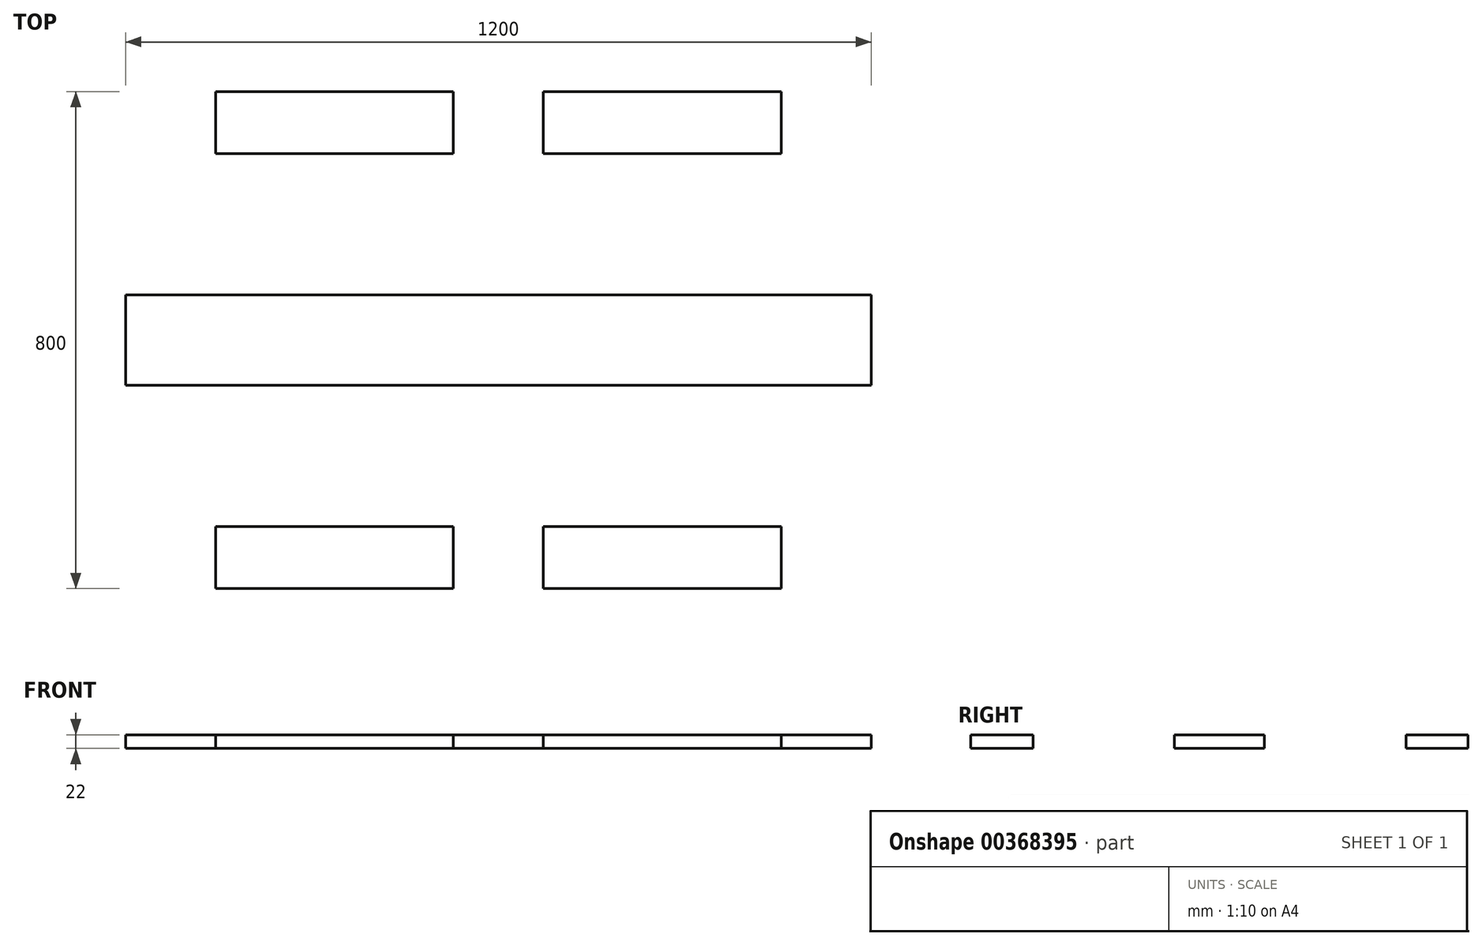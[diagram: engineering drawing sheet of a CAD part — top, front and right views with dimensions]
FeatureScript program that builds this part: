
annotation { "Feature Type Name" : "Feature", "Feature Type Description" : "" }
export const myFeature = defineFeature(function(context is Context, id is Id, definition is map)
    precondition{}
    {
        {
            var Q0;
            Q0=qCreatedBy(makeId("Top.planeOp"),FACE);
            var sketch = newSketch(context, id + "F0", { "sketchPlane" : qUnion([Q0])});
            skLineSegment(sketch, "E0.bottom", {"start": v(600, 400) * mm, "end": v(-600, 400) * mm, "construction": true});
            skLineSegment(sketch, "E0.top", {"start": v(600, -400) * mm, "end": v(-600, -400) * mm, "construction": true});
            skLineSegment(sketch, "E0.left", {"start": v(600, 400) * mm, "end": v(600, -400) * mm, "construction": true});
            skLineSegment(sketch, "E0.right", {"start": v(-600, 400) * mm, "end": v(-600, -400) * mm, "construction": true});
            skPoint(sketch, "E0.middle", {"position": v(0, 0) * mm});
            skLineSegment(sketch, "E1.left", {"start": v(-600, -400) * mm, "end": v(-600, -400) * mm});
            skLineSegment(sketch, "E1.right", {"start": v(600, -400) * mm, "end": v(600, -400) * mm});
            skLineSegment(sketch, "E2.bottom", {"start": v(-600, -400) * mm, "end": v(600, -400) * mm});
            skLineSegment(sketch, "E2.top", {"start": v(-600, -300) * mm, "end": v(600, -300) * mm});
            skLineSegment(sketch, "E2.left", {"start": v(-600, -400) * mm, "end": v(-600, -300) * mm});
            skLineSegment(sketch, "E2.right", {"start": v(600, -400) * mm, "end": v(600, -300) * mm});
            skLineSegment(sketch, "E3.bottom", {"start": v(-600, 400) * mm, "end": v(600, 400) * mm});
            skLineSegment(sketch, "E3.top", {"start": v(-600, 300) * mm, "end": v(600, 300) * mm});
            skLineSegment(sketch, "E3.left", {"start": v(-600, 400) * mm, "end": v(-600, 300) * mm});
            skLineSegment(sketch, "E3.right", {"start": v(600, 400) * mm, "end": v(600, 300) * mm});
            skLineSegment(sketch, "E4.bottom", {"start": v(-600, 72.5) * mm, "end": v(600, 72.5) * mm});
            skLineSegment(sketch, "E4.top", {"start": v(-600, -72.5) * mm, "end": v(600, -72.5) * mm});
            skLineSegment(sketch, "E4.left", {"start": v(-600, 72.5) * mm, "end": v(-600, -72.5) * mm});
            skLineSegment(sketch, "E4.right", {"start": v(600, 72.5) * mm, "end": v(600, -72.5) * mm});
            skLineSegment(sketch, "E5.bottom", {"start": v(-600, 260) * mm, "end": v(600, 260) * mm});
            skLineSegment(sketch, "E5.top", {"start": v(-600, 160) * mm, "end": v(600, 160) * mm});
            skLineSegment(sketch, "E5.left", {"start": v(-600, 260) * mm, "end": v(-600, 160) * mm});
            skLineSegment(sketch, "E5.right", {"start": v(600, 260) * mm, "end": v(600, 160) * mm});
            skLineSegment(sketch, "E6.bottom", {"start": v(-600, -160) * mm, "end": v(600, -160) * mm});
            skLineSegment(sketch, "E6.top", {"start": v(-600, -260) * mm, "end": v(600, -260) * mm});
            skLineSegment(sketch, "E6.left", {"start": v(-600, -160) * mm, "end": v(-600, -260) * mm});
            skLineSegment(sketch, "E6.right", {"start": v(600, -160) * mm, "end": v(600, -260) * mm});
            skLineSegment(sketch, "E7.bottom", {"start": v(-600, 400) * mm, "end": v(-455, 400) * mm});
            skLineSegment(sketch, "E7.top", {"start": v(-600, -400) * mm, "end": v(-455, -400) * mm});
            skLineSegment(sketch, "E7.left", {"start": v(-600, 400) * mm, "end": v(-600, -400) * mm});
            skLineSegment(sketch, "E7.right", {"start": v(-455, 400) * mm, "end": v(-455, -400) * mm});
            skLineSegment(sketch, "E8.bottom", {"start": v(600, 400) * mm, "end": v(455, 400) * mm});
            skLineSegment(sketch, "E8.top", {"start": v(600, -400) * mm, "end": v(455, -400) * mm});
            skLineSegment(sketch, "E8.left", {"start": v(600, 400) * mm, "end": v(600, -400) * mm});
            skLineSegment(sketch, "E8.right", {"start": v(455, 400) * mm, "end": v(455, -400) * mm});
            skLineSegment(sketch, "E9.bottom", {"start": v(72, -400) * mm, "end": v(-73, -400) * mm});
            skLineSegment(sketch, "E9.top", {"start": v(72, 400) * mm, "end": v(-73, 400) * mm});
            skLineSegment(sketch, "E9.left", {"start": v(72, -400) * mm, "end": v(72, 400) * mm});
            skLineSegment(sketch, "E9.right", {"start": v(-73, -400) * mm, "end": v(-73, 400) * mm});
            skPoint(sketch, "E9.middle", {"position": v(-0.5, 0) * mm});
            skSolve(sketch);
        }
        {
            var Q0;
            {var subQ5=sQuery(id+"F0.wireOp",EDGE,"E8.bottom");Q0=makeQuery(id+"F0.imprint","IMPRINT",FACE,{"disambiguationData":[TD([[makeQuery(id+"F0.imprint","IMPRINT",EDGE,{"derivedFrom":subQ5}),1.0]])]});}
            var Q1;
            {var subQ3=sQuery(id+"F0.wireOp",EDGE,"E9.left");var subQ5=sQuery(id+"F0.wireOp",EDGE,"E3.top");var subQ6=makeQuery(id+"F0.imprint","INTERSECT",VERTEX,{"derivedFrom":[subQ5,subQ3]});Q1=makeQuery(id+"F0.imprint","IMPRINT",FACE,{"disambiguationData":[TD([[makeQuery(id+"F0.imprint","IMPRINT",EDGE,{"disambiguationData":[TD([[subQ6,-1.0]])],"derivedFrom":subQ5}),1.0]])]});}
            var Q2;
            {var subQ5=sQuery(id+"F0.wireOp",EDGE,"E9.top");Q2=makeQuery(id+"F0.imprint","IMPRINT",FACE,{"disambiguationData":[TD([[makeQuery(id+"F0.imprint","IMPRINT",EDGE,{"derivedFrom":subQ5}),1.0]])]});}
            var Q3;
            {var subQ0=sQuery(id+"F0.wireOp",EDGE,"E7.right");var subQ5=sQuery(id+"F0.wireOp",EDGE,"E3.top");var subQ6=makeQuery(id+"F0.imprint","INTERSECT",VERTEX,{"derivedFrom":[subQ5,subQ0]});Q3=makeQuery(id+"F0.imprint","IMPRINT",FACE,{"disambiguationData":[TD([[makeQuery(id+"F0.imprint","IMPRINT",EDGE,{"disambiguationData":[TD([[subQ6,-1.0]])],"derivedFrom":subQ5}),1.0]])]});}
            var Q4;
            {var subQ5=sQuery(id+"F0.wireOp",EDGE,"E7.bottom");Q4=makeQuery(id+"F0.imprint","IMPRINT",FACE,{"disambiguationData":[TD([[makeQuery(id+"F0.imprint","IMPRINT",EDGE,{"derivedFrom":subQ5}),-1.0]])]});}
            var Q5;
            {var subQ0=sQuery(id+"F0.wireOp",EDGE,"E7.left");var subQ1=sQuery(id+"F0.wireOp",EDGE,"E5.bottom");var subQ2=makeQuery(id+"F0.imprint","INTERSECT",VERTEX,{"derivedFrom":[subQ1,subQ0]});Q5=makeQuery(id+"F0.imprint","IMPRINT",FACE,{"disambiguationData":[TD([[makeQuery(id+"F0.imprint","IMPRINT",EDGE,{"disambiguationData":[TD([[subQ2,-1.0]])],"derivedFrom":subQ1}),-1.0]])]});}
            var Q6;
            {var subQ0=sQuery(id+"F0.wireOp",EDGE,"E7.right");var subQ1=sQuery(id+"F0.wireOp",EDGE,"E5.bottom");var subQ2=makeQuery(id+"F0.imprint","INTERSECT",VERTEX,{"derivedFrom":[subQ1,subQ0]});Q6=makeQuery(id+"F0.imprint","IMPRINT",FACE,{"disambiguationData":[TD([[makeQuery(id+"F0.imprint","IMPRINT",EDGE,{"disambiguationData":[TD([[subQ2,-1.0]])],"derivedFrom":subQ1}),-1.0]])]});}
            var Q7;
            {var subQ0=sQuery(id+"F0.wireOp",EDGE,"E9.right");var subQ1=sQuery(id+"F0.wireOp",EDGE,"E5.bottom");var subQ2=makeQuery(id+"F0.imprint","INTERSECT",VERTEX,{"derivedFrom":[subQ1,subQ0]});Q7=makeQuery(id+"F0.imprint","IMPRINT",FACE,{"disambiguationData":[TD([[makeQuery(id+"F0.imprint","IMPRINT",EDGE,{"disambiguationData":[TD([[subQ2,-1.0]])],"derivedFrom":subQ1}),-1.0]])]});}
            var Q8;
            {var subQ0=sQuery(id+"F0.wireOp",EDGE,"E9.left");var subQ1=sQuery(id+"F0.wireOp",EDGE,"E5.bottom");var subQ2=makeQuery(id+"F0.imprint","INTERSECT",VERTEX,{"derivedFrom":[subQ1,subQ0]});Q8=makeQuery(id+"F0.imprint","IMPRINT",FACE,{"disambiguationData":[TD([[makeQuery(id+"F0.imprint","IMPRINT",EDGE,{"disambiguationData":[TD([[subQ2,-1.0]])],"derivedFrom":subQ1}),-1.0]])]});}
            var Q9;
            {var subQ0=sQuery(id+"F0.wireOp",EDGE,"E8.left");var subQ1=sQuery(id+"F0.wireOp",EDGE,"E5.bottom");var subQ2=makeQuery(id+"F0.imprint","INTERSECT",VERTEX,{"derivedFrom":[subQ1,subQ0]});Q9=makeQuery(id+"F0.imprint","IMPRINT",FACE,{"disambiguationData":[TD([[makeQuery(id+"F0.imprint","IMPRINT",EDGE,{"disambiguationData":[TD([[subQ2,1.0]])],"derivedFrom":subQ1}),-1.0]])]});}
            var Q10;
            {var subQ0=sQuery(id+"F0.wireOp",EDGE,"E8.left");var subQ1=sQuery(id+"F0.wireOp",EDGE,"E4.bottom");var subQ2=makeQuery(id+"F0.imprint","INTERSECT",VERTEX,{"derivedFrom":[subQ1,subQ0]});Q10=makeQuery(id+"F0.imprint","IMPRINT",FACE,{"disambiguationData":[TD([[makeQuery(id+"F0.imprint","IMPRINT",EDGE,{"disambiguationData":[TD([[subQ2,1.0]])],"derivedFrom":subQ1}),-1.0]])]});}
            var Q11;
            {var subQ0=sQuery(id+"F0.wireOp",EDGE,"E9.left");var subQ1=sQuery(id+"F0.wireOp",EDGE,"E4.bottom");var subQ2=makeQuery(id+"F0.imprint","INTERSECT",VERTEX,{"derivedFrom":[subQ1,subQ0]});Q11=makeQuery(id+"F0.imprint","IMPRINT",FACE,{"disambiguationData":[TD([[makeQuery(id+"F0.imprint","IMPRINT",EDGE,{"disambiguationData":[TD([[subQ2,-1.0]])],"derivedFrom":subQ1}),-1.0]])]});}
            var Q12;
            {var subQ0=sQuery(id+"F0.wireOp",EDGE,"E9.right");var subQ1=sQuery(id+"F0.wireOp",EDGE,"E4.bottom");var subQ2=makeQuery(id+"F0.imprint","INTERSECT",VERTEX,{"derivedFrom":[subQ1,subQ0]});Q12=makeQuery(id+"F0.imprint","IMPRINT",FACE,{"disambiguationData":[TD([[makeQuery(id+"F0.imprint","IMPRINT",EDGE,{"disambiguationData":[TD([[subQ2,-1.0]])],"derivedFrom":subQ1}),-1.0]])]});}
            var Q13;
            {var subQ0=sQuery(id+"F0.wireOp",EDGE,"E7.right");var subQ1=sQuery(id+"F0.wireOp",EDGE,"E4.bottom");var subQ2=makeQuery(id+"F0.imprint","INTERSECT",VERTEX,{"derivedFrom":[subQ1,subQ0]});Q13=makeQuery(id+"F0.imprint","IMPRINT",FACE,{"disambiguationData":[TD([[makeQuery(id+"F0.imprint","IMPRINT",EDGE,{"disambiguationData":[TD([[subQ2,-1.0]])],"derivedFrom":subQ1}),-1.0]])]});}
            var Q14;
            {var subQ0=sQuery(id+"F0.wireOp",EDGE,"E7.left");var subQ1=sQuery(id+"F0.wireOp",EDGE,"E4.bottom");var subQ2=makeQuery(id+"F0.imprint","INTERSECT",VERTEX,{"derivedFrom":[subQ1,subQ0]});Q14=makeQuery(id+"F0.imprint","IMPRINT",FACE,{"disambiguationData":[TD([[makeQuery(id+"F0.imprint","IMPRINT",EDGE,{"disambiguationData":[TD([[subQ2,-1.0]])],"derivedFrom":subQ1}),-1.0]])]});}
            var Q15;
            {var subQ0=sQuery(id+"F0.wireOp",EDGE,"E7.left");var subQ1=sQuery(id+"F0.wireOp",EDGE,"E6.bottom");var subQ2=makeQuery(id+"F0.imprint","INTERSECT",VERTEX,{"derivedFrom":[subQ1,subQ0]});Q15=makeQuery(id+"F0.imprint","IMPRINT",FACE,{"disambiguationData":[TD([[makeQuery(id+"F0.imprint","IMPRINT",EDGE,{"disambiguationData":[TD([[subQ2,-1.0]])],"derivedFrom":subQ1}),-1.0]])]});}
            var Q16;
            {var subQ0=sQuery(id+"F0.wireOp",EDGE,"E7.right");var subQ1=sQuery(id+"F0.wireOp",EDGE,"E6.bottom");var subQ2=makeQuery(id+"F0.imprint","INTERSECT",VERTEX,{"derivedFrom":[subQ1,subQ0]});Q16=makeQuery(id+"F0.imprint","IMPRINT",FACE,{"disambiguationData":[TD([[makeQuery(id+"F0.imprint","IMPRINT",EDGE,{"disambiguationData":[TD([[subQ2,-1.0]])],"derivedFrom":subQ1}),-1.0]])]});}
            var Q17;
            {var subQ0=sQuery(id+"F0.wireOp",EDGE,"E9.right");var subQ1=sQuery(id+"F0.wireOp",EDGE,"E6.bottom");var subQ2=makeQuery(id+"F0.imprint","INTERSECT",VERTEX,{"derivedFrom":[subQ1,subQ0]});Q17=makeQuery(id+"F0.imprint","IMPRINT",FACE,{"disambiguationData":[TD([[makeQuery(id+"F0.imprint","IMPRINT",EDGE,{"disambiguationData":[TD([[subQ2,-1.0]])],"derivedFrom":subQ1}),-1.0]])]});}
            var Q18;
            {var subQ0=sQuery(id+"F0.wireOp",EDGE,"E9.left");var subQ1=sQuery(id+"F0.wireOp",EDGE,"E6.bottom");var subQ2=makeQuery(id+"F0.imprint","INTERSECT",VERTEX,{"derivedFrom":[subQ1,subQ0]});Q18=makeQuery(id+"F0.imprint","IMPRINT",FACE,{"disambiguationData":[TD([[makeQuery(id+"F0.imprint","IMPRINT",EDGE,{"disambiguationData":[TD([[subQ2,-1.0]])],"derivedFrom":subQ1}),-1.0]])]});}
            var Q19;
            {var subQ0=sQuery(id+"F0.wireOp",EDGE,"E8.left");var subQ1=sQuery(id+"F0.wireOp",EDGE,"E6.bottom");var subQ2=makeQuery(id+"F0.imprint","INTERSECT",VERTEX,{"derivedFrom":[subQ1,subQ0]});Q19=makeQuery(id+"F0.imprint","IMPRINT",FACE,{"disambiguationData":[TD([[makeQuery(id+"F0.imprint","IMPRINT",EDGE,{"disambiguationData":[TD([[subQ2,1.0]])],"derivedFrom":subQ1}),-1.0]])]});}
            var Q20;
            {var subQ5=sQuery(id+"F0.wireOp",EDGE,"E8.top");Q20=makeQuery(id+"F0.imprint","IMPRINT",FACE,{"disambiguationData":[TD([[makeQuery(id+"F0.imprint","IMPRINT",EDGE,{"derivedFrom":subQ5}),-1.0]])]});}
            var Q21;
            {var subQ3=sQuery(id+"F0.wireOp",EDGE,"E9.left");var subQ5=sQuery(id+"F0.wireOp",EDGE,"E2.top");var subQ6=makeQuery(id+"F0.imprint","INTERSECT",VERTEX,{"derivedFrom":[subQ5,subQ3]});Q21=makeQuery(id+"F0.imprint","IMPRINT",FACE,{"disambiguationData":[TD([[makeQuery(id+"F0.imprint","IMPRINT",EDGE,{"disambiguationData":[TD([[subQ6,-1.0]])],"derivedFrom":subQ5}),-1.0]])]});}
            var Q22;
            {var subQ5=sQuery(id+"F0.wireOp",EDGE,"E9.bottom");Q22=makeQuery(id+"F0.imprint","IMPRINT",FACE,{"disambiguationData":[TD([[makeQuery(id+"F0.imprint","IMPRINT",EDGE,{"derivedFrom":subQ5}),-1.0]])]});}
            var Q23;
            {var subQ0=sQuery(id+"F0.wireOp",EDGE,"E7.right");var subQ5=sQuery(id+"F0.wireOp",EDGE,"E2.top");var subQ7=makeQuery(id+"F0.imprint","INTERSECT",VERTEX,{"derivedFrom":[subQ5,subQ0]});Q23=makeQuery(id+"F0.imprint","IMPRINT",FACE,{"disambiguationData":[TD([[makeQuery(id+"F0.imprint","IMPRINT",EDGE,{"disambiguationData":[TD([[subQ7,-1.0]])],"derivedFrom":subQ5}),-1.0]])]});}
            var Q24;
            {var subQ5=sQuery(id+"F0.wireOp",EDGE,"E7.top");Q24=makeQuery(id+"F0.imprint","IMPRINT",FACE,{"disambiguationData":[TD([[makeQuery(id+"F0.imprint","IMPRINT",EDGE,{"derivedFrom":subQ5}),1.0]])]});}
            extrude(context, id + "F1", {"entities" : qUnion([Q0, Q1, Q2, Q3, Q4, Q5, Q6, Q7, Q8, Q9, Q10, Q11, Q12, Q13, Q14, Q15, Q16, Q17, Q18, Q19, Q20, Q21, Q22, Q23, Q24]), "depth" : 22 * mm});
        }
        {
            var Q0;
            Q0=makeQuery(id+"F1.opExtrude","SWEPT_BODY",BODY,{"disambiguationData":[OSD([sQuery(id+"F0.wireOp",EDGE,"E6.bottom"),sQuery(id+"F0.wireOp",EDGE,"E6.top"),sQuery(id+"F0.wireOp",EDGE,"E7.left"),sQuery(id+"F0.wireOp",EDGE,"E8.left")])]});
            var Q1;
            Q1=makeQuery(id+"F1.opExtrude","SWEPT_BODY",BODY,{"disambiguationData":[OSD([sQuery(id+"F0.wireOp",EDGE,"E5.bottom"),sQuery(id+"F0.wireOp",EDGE,"E5.top"),sQuery(id+"F0.wireOp",EDGE,"E7.left"),sQuery(id+"F0.wireOp",EDGE,"E8.left")])]});
            deleteBodies(context, id + "F2", {"entities" : qUnion([Q0, Q1])});
        }
        {
            var Q0;
            Q0=makeQuery(id+"F1.opExtrude","SWEPT_BODY",BODY,{"disambiguationData":[OSD([sQuery(id+"F0.wireOp",EDGE,"E3.bottom"),sQuery(id+"F0.wireOp",EDGE,"E3.top"),sQuery(id+"F0.wireOp",EDGE,"E7.bottom"),sQuery(id+"F0.wireOp",EDGE,"E7.left"),sQuery(id+"F0.wireOp",EDGE,"E8.bottom"),sQuery(id+"F0.wireOp",EDGE,"E8.left"),sQuery(id+"F0.wireOp",EDGE,"E9.top")])]});
            var Q1;
            Q1=makeQuery(id+"F1.opExtrude","SWEPT_BODY",BODY,{"disambiguationData":[OSD([sQuery(id+"F0.wireOp",EDGE,"E2.bottom"),sQuery(id+"F0.wireOp",EDGE,"E2.top"),sQuery(id+"F0.wireOp",EDGE,"E7.top"),sQuery(id+"F0.wireOp",EDGE,"E7.left"),sQuery(id+"F0.wireOp",EDGE,"E8.top"),sQuery(id+"F0.wireOp",EDGE,"E8.left"),sQuery(id+"F0.wireOp",EDGE,"E9.bottom")])]});
            deleteBodies(context, id + "F3", {"entities" : qUnion([Q0, Q1])});
        }
        {
            var Q0;
            {var subQ5=sQuery(id+"F0.wireOp",EDGE,"E8.bottom");Q0=makeQuery(id+"F0.imprint","IMPRINT",FACE,{"disambiguationData":[TD([[makeQuery(id+"F0.imprint","IMPRINT",EDGE,{"derivedFrom":subQ5}),1.0]])]});}
            var Q1;
            {var subQ3=sQuery(id+"F0.wireOp",EDGE,"E9.left");var subQ5=sQuery(id+"F0.wireOp",EDGE,"E3.top");var subQ6=makeQuery(id+"F0.imprint","INTERSECT",VERTEX,{"derivedFrom":[subQ5,subQ3]});Q1=makeQuery(id+"F0.imprint","IMPRINT",FACE,{"disambiguationData":[TD([[makeQuery(id+"F0.imprint","IMPRINT",EDGE,{"disambiguationData":[TD([[subQ6,-1.0]])],"derivedFrom":subQ5}),1.0]])]});}
            var Q2;
            {var subQ5=sQuery(id+"F0.wireOp",EDGE,"E9.top");Q2=makeQuery(id+"F0.imprint","IMPRINT",FACE,{"disambiguationData":[TD([[makeQuery(id+"F0.imprint","IMPRINT",EDGE,{"derivedFrom":subQ5}),1.0]])]});}
            var Q3;
            {var subQ0=sQuery(id+"F0.wireOp",EDGE,"E7.right");var subQ5=sQuery(id+"F0.wireOp",EDGE,"E3.top");var subQ6=makeQuery(id+"F0.imprint","INTERSECT",VERTEX,{"derivedFrom":[subQ5,subQ0]});Q3=makeQuery(id+"F0.imprint","IMPRINT",FACE,{"disambiguationData":[TD([[makeQuery(id+"F0.imprint","IMPRINT",EDGE,{"disambiguationData":[TD([[subQ6,-1.0]])],"derivedFrom":subQ5}),1.0]])]});}
            var Q4;
            {var subQ5=sQuery(id+"F0.wireOp",EDGE,"E7.bottom");Q4=makeQuery(id+"F0.imprint","IMPRINT",FACE,{"disambiguationData":[TD([[makeQuery(id+"F0.imprint","IMPRINT",EDGE,{"derivedFrom":subQ5}),-1.0]])]});}
            var Q5;
            {var subQ5=sQuery(id+"F0.wireOp",EDGE,"E7.top");Q5=makeQuery(id+"F0.imprint","IMPRINT",FACE,{"disambiguationData":[TD([[makeQuery(id+"F0.imprint","IMPRINT",EDGE,{"derivedFrom":subQ5}),1.0]])]});}
            var Q6;
            {var subQ0=sQuery(id+"F0.wireOp",EDGE,"E7.right");var subQ5=sQuery(id+"F0.wireOp",EDGE,"E2.top");var subQ7=makeQuery(id+"F0.imprint","INTERSECT",VERTEX,{"derivedFrom":[subQ5,subQ0]});Q6=makeQuery(id+"F0.imprint","IMPRINT",FACE,{"disambiguationData":[TD([[makeQuery(id+"F0.imprint","IMPRINT",EDGE,{"disambiguationData":[TD([[subQ7,-1.0]])],"derivedFrom":subQ5}),-1.0]])]});}
            var Q7;
            {var subQ5=sQuery(id+"F0.wireOp",EDGE,"E9.bottom");Q7=makeQuery(id+"F0.imprint","IMPRINT",FACE,{"disambiguationData":[TD([[makeQuery(id+"F0.imprint","IMPRINT",EDGE,{"derivedFrom":subQ5}),-1.0]])]});}
            var Q8;
            {var subQ3=sQuery(id+"F0.wireOp",EDGE,"E9.left");var subQ5=sQuery(id+"F0.wireOp",EDGE,"E2.top");var subQ6=makeQuery(id+"F0.imprint","INTERSECT",VERTEX,{"derivedFrom":[subQ5,subQ3]});Q8=makeQuery(id+"F0.imprint","IMPRINT",FACE,{"disambiguationData":[TD([[makeQuery(id+"F0.imprint","IMPRINT",EDGE,{"disambiguationData":[TD([[subQ6,-1.0]])],"derivedFrom":subQ5}),-1.0]])]});}
            var Q9;
            {var subQ5=sQuery(id+"F0.wireOp",EDGE,"E8.top");Q9=makeQuery(id+"F0.imprint","IMPRINT",FACE,{"disambiguationData":[TD([[makeQuery(id+"F0.imprint","IMPRINT",EDGE,{"derivedFrom":subQ5}),-1.0]])]});}
            extrude(context, id + "F4", {"entities" : qUnion([Q0, Q1, Q2, Q3, Q4, Q5, Q6, Q7, Q8, Q9]), "depth" : 22 * mm});
        }
    });
